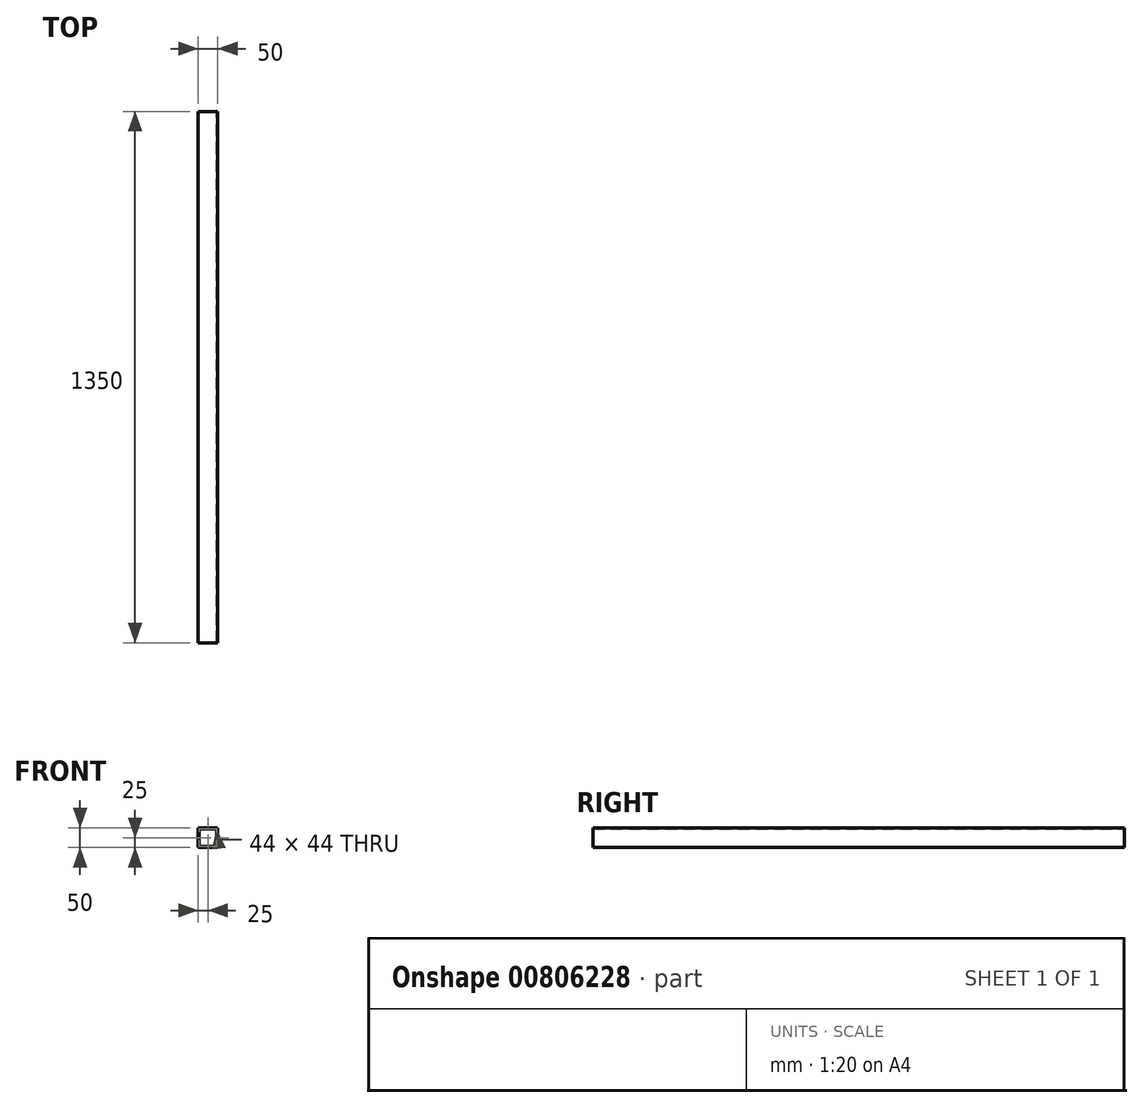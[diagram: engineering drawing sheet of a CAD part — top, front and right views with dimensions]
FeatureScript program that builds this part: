
annotation { "Feature Type Name" : "Feature", "Feature Type Description" : "" }
export const myFeature = defineFeature(function(context is Context, id is Id, definition is map)
    precondition{}
    {
        {
            var Q0;
            Q0=qCreatedBy(makeId("Front.planeOp"),FACE);
            var sketch = newSketch(context, id + "F0", { "sketchPlane" : qUnion([Q0])});
            skLineSegment(sketch, "E0.bottom", {"start": v(25, -25) * mm, "end": v(-25, -25) * mm});
            skLineSegment(sketch, "E0.top", {"start": v(25, 25) * mm, "end": v(-25, 25) * mm});
            skLineSegment(sketch, "E0.left", {"start": v(25, -25) * mm, "end": v(25, 25) * mm});
            skLineSegment(sketch, "E0.right", {"start": v(-25, -25) * mm, "end": v(-25, 25) * mm});
            skPoint(sketch, "E0.middle", {"position": v(0, 0) * mm});
            skLineSegment(sketch, "E1.0", {"start": v(-22, -22) * mm, "end": v(-22, 22) * mm});
            skLineSegment(sketch, "E1.1", {"start": v(22, -22) * mm, "end": v(-22, -22) * mm});
            skLineSegment(sketch, "E1.2", {"start": v(22, -22) * mm, "end": v(22, 22) * mm});
            skLineSegment(sketch, "E1.3", {"start": v(22, 22) * mm, "end": v(-22, 22) * mm});
            skSolve(sketch);
        }
        {
            var Q0;
            Q0=qSketchRegion(id+"F0",true);
            extrude(context, id + "F1", {"entities" : qUnion([Q0]), "depth" : 1350 * mm, "offsetDistance" : 25 * mm});
        }
    });
